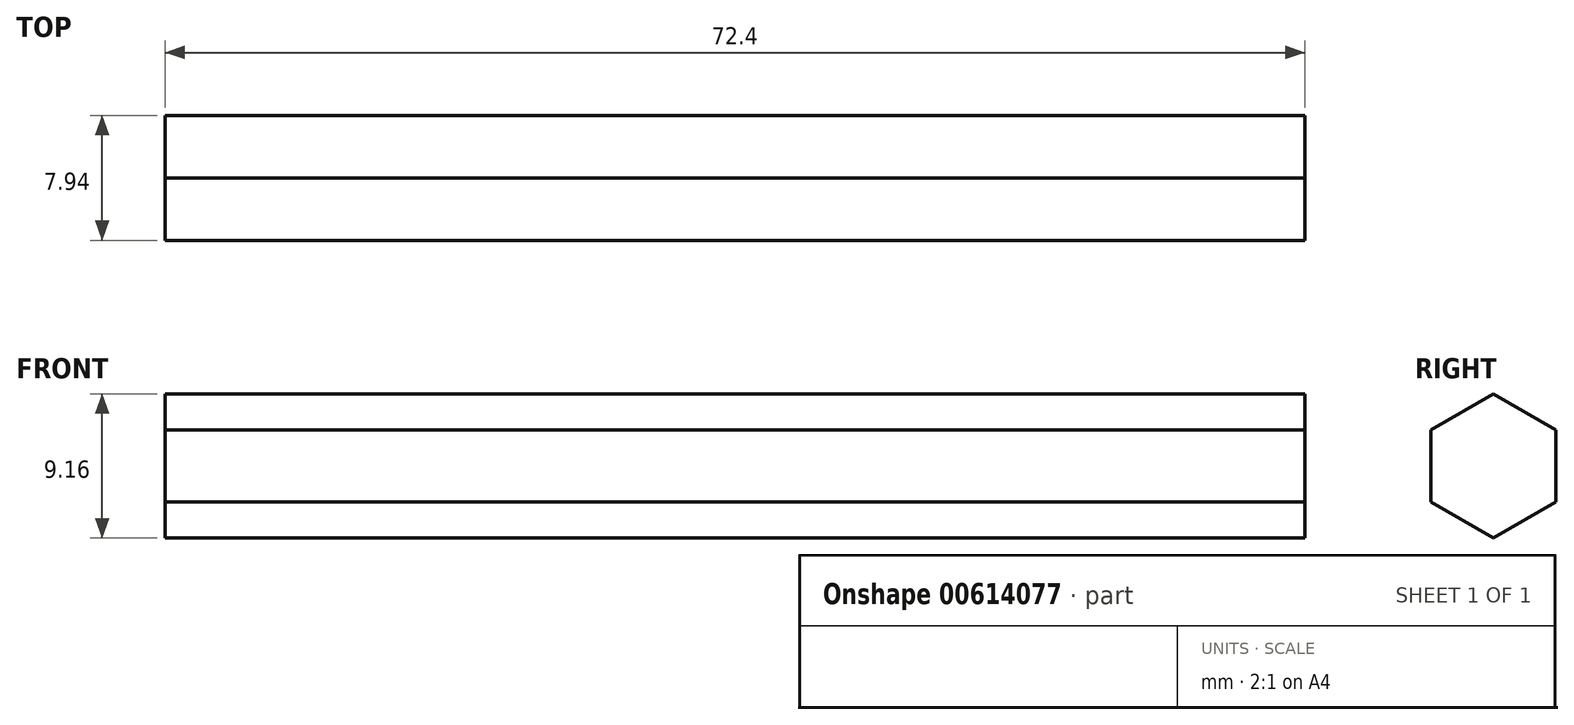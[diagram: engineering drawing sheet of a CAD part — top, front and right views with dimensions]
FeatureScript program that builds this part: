
annotation { "Feature Type Name" : "Feature", "Feature Type Description" : "" }
export const myFeature = defineFeature(function(context is Context, id is Id, definition is map)
    precondition{}
    {
        {
            var Q0;
            Q0=qCreatedBy(makeId("Right.planeOp"),FACE);
            var sketch = newSketch(context, id + "F0", { "sketchPlane" : qUnion([Q0])});
            skCircle(sketch, "E0.cCircle", {"center": v(0, 0) * mm, "radius": 3.97 * mm, "construction": true});
            skLineSegment(sketch, "E0.0", {"start": v(3.97, -2.3) * mm, "end": v(0, -4.58) * mm});
            skLineSegment(sketch, "E0.1", {"start": v(0, -4.58) * mm, "end": v(-3.97, -2.3) * mm});
            skLineSegment(sketch, "E0.2", {"start": v(-3.97, -2.3) * mm, "end": v(-3.97, 2.3) * mm});
            skLineSegment(sketch, "E0.3", {"start": v(-3.97, 2.3) * mm, "end": v(0, 4.58) * mm});
            skLineSegment(sketch, "E0.4", {"start": v(0, 4.58) * mm, "end": v(3.97, 2.3) * mm});
            skLineSegment(sketch, "E0.5", {"start": v(3.97, 2.3) * mm, "end": v(3.97, -2.3) * mm});
            skPoint(sketch, "E0.0.midPoint", {"position": v(1.98, -3.44) * mm});
            skSolve(sketch);
        }
        {
            var Q0;
            Q0=makeQuery(id+"F0.imprint","IMPRINT",FACE,{"disambiguationData":[TD([[makeQuery(id+"F0.imprint","IMPRINT",EDGE,{"derivedFrom":sQuery(id+"F0.wireOp",EDGE,"E0.0")}),-1.0]])]});
            extrude(context, id + "F1", {"entities" : qUnion([Q0]), "endBound" : BoundingType.SYMMETRIC, "depth" : 72.39 * mm, "offsetDistance" : 25.4 * mm});
        }
    });
